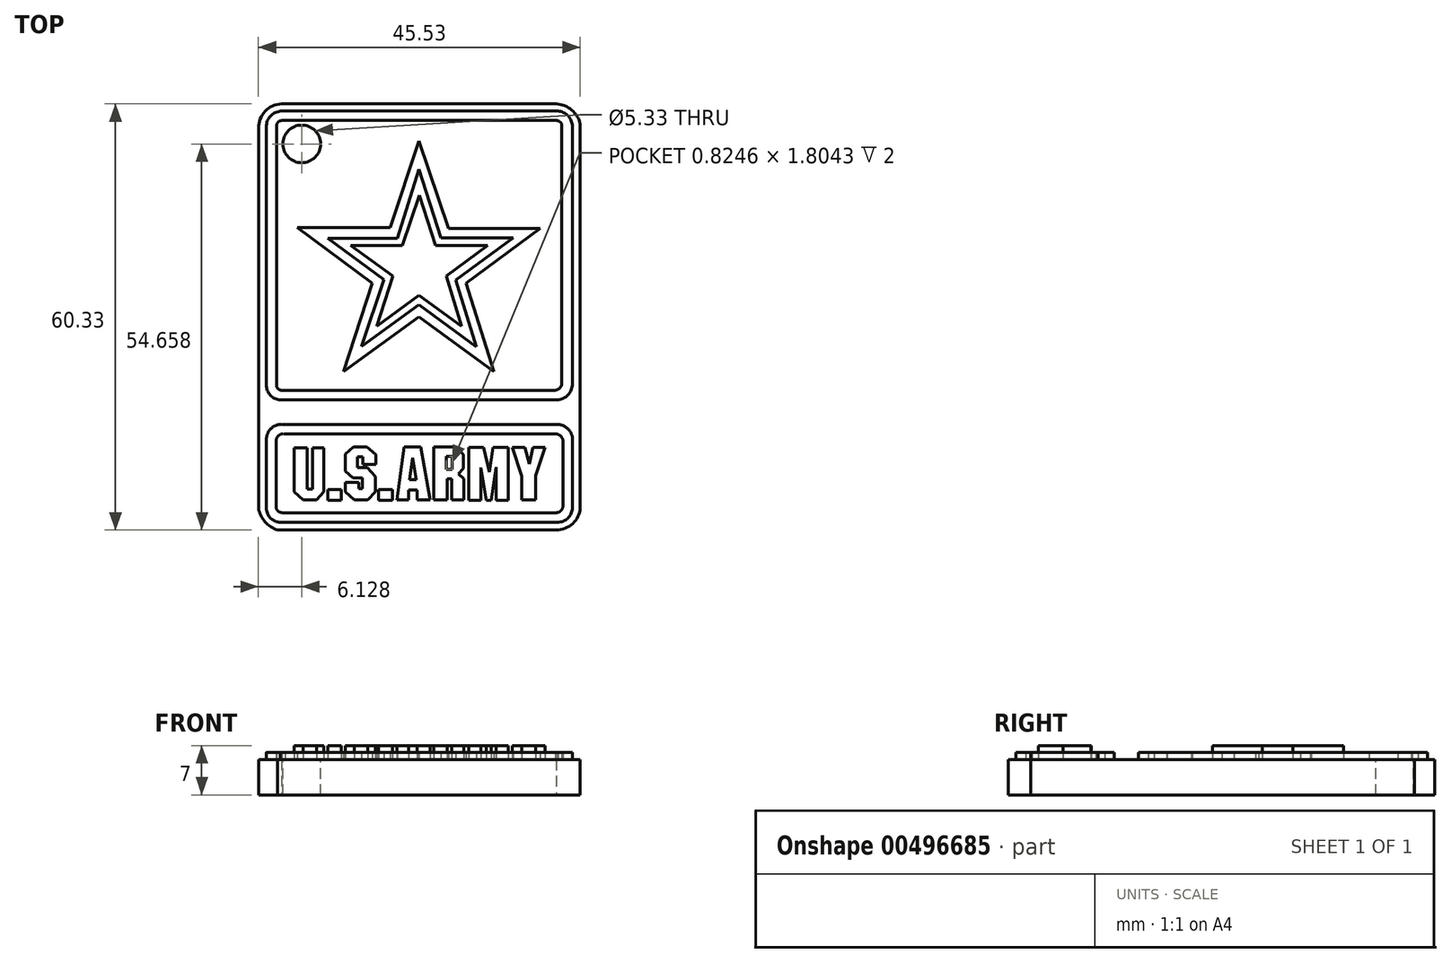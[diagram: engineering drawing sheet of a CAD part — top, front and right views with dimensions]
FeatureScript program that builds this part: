
annotation { "Feature Type Name" : "Feature", "Feature Type Description" : "" }
export const myFeature = defineFeature(function(context is Context, id is Id, definition is map)
    precondition{}
    {
        {
            var Q0;
            Q0=qCreatedBy(makeId("Top.planeOp"),FACE);
            var sketch = newSketch(context, id + "F0", { "sketchPlane" : qUnion([Q0])});
            skLineSegment(sketch, "E0", {"start": v(-59.52, 64.35) * mm, "end": v(-59.52, 10.5) * mm});
            skArc(sketch, "E1", {"start": v(-59.52, 10.5) * mm, "mid": v(-58.58, 8.6) * mm, "end": v(-56.8, 7.44) * mm});
            skLineSegment(sketch, "E2", {"start": v(-56.8, 7.44) * mm, "end": v(-17.38, 7.44) * mm});
            skArc(sketch, "E3", {"start": v(-17.38, 7.44) * mm, "mid": v(-15.06, 8.35) * mm, "end": v(-13.99, 10.6) * mm});
            skLineSegment(sketch, "E4", {"start": v(-13.99, 10.6) * mm, "end": v(-13.99, 64.9) * mm});
            skArc(sketch, "E5", {"start": v(-13.99, 64.9) * mm, "mid": v(-15.21, 66.9) * mm, "end": v(-17.38, 67.77) * mm});
            skLineSegment(sketch, "E6", {"start": v(-17.38, 67.77) * mm, "end": v(-56.25, 67.77) * mm});
            skArc(sketch, "E7", {"start": v(-56.25, 67.77) * mm, "mid": v(-58.57, 66.71) * mm, "end": v(-59.52, 64.35) * mm});
            skSolve(sketch);
        }
        {
            var Q0;
            Q0=makeQuery(id+"F0.imprint","IMPRINT",FACE,{"disambiguationData":[TD([[makeQuery(id+"F0.imprint","IMPRINT",EDGE,{"derivedFrom":sQuery(id+"F0.wireOp",EDGE,"E0")}),1.0]])]});
            var sketch = newSketch(context, id + "F1", { "sketchPlane" : qUnion([Q0])});
            skLineSegment(sketch, "E8", {"start": v(-58.4, 64.53) * mm, "end": v(-58.4, 28) * mm});
            skLineSegment(sketch, "E9", {"start": v(-56.4, 25.84) * mm, "end": v(-17.26, 25.84) * mm});
            skLineSegment(sketch, "E10", {"start": v(-15.1, 28.14) * mm, "end": v(-15.1, 64.56) * mm});
            skLineSegment(sketch, "E11", {"start": v(-17.16, 66.74) * mm, "end": v(-56.36, 66.74) * mm});
            skArc(sketch, "E12", {"start": v(-56.36, 66.74) * mm, "mid": v(-57.82, 66.04) * mm, "end": v(-58.4, 64.53) * mm});
            skArc(sketch, "E13", {"start": v(-58.4, 28) * mm, "mid": v(-57.83, 26.52) * mm, "end": v(-56.4, 25.84) * mm});
            skArc(sketch, "E14", {"start": v(-17.26, 25.84) * mm, "mid": v(-15.73, 26.57) * mm, "end": v(-15.1, 28.14) * mm});
            skArc(sketch, "E15", {"start": v(-15.1, 64.56) * mm, "mid": v(-15.7, 66.05) * mm, "end": v(-17.16, 66.74) * mm});
            skLineSegment(sketch, "E16", {"start": v(-56.18, 65.4) * mm, "end": v(-17.37, 65.4) * mm});
            skLineSegment(sketch, "E17", {"start": v(-16.61, 64.46) * mm, "end": v(-16.61, 28.23) * mm});
            skLineSegment(sketch, "E18", {"start": v(-17.54, 27.23) * mm, "end": v(-56.23, 27.23) * mm});
            skLineSegment(sketch, "E19", {"start": v(-56.96, 28.09) * mm, "end": v(-56.96, 64.55) * mm});
            skArc(sketch, "E20", {"start": v(-56.18, 65.4) * mm, "mid": v(-56.76, 65.15) * mm, "end": v(-56.96, 64.55) * mm});
            skArc(sketch, "E21", {"start": v(-16.61, 64.46) * mm, "mid": v(-16.76, 65.12) * mm, "end": v(-17.37, 65.4) * mm});
            skArc(sketch, "E22", {"start": v(-17.54, 27.23) * mm, "mid": v(-16.88, 27.55) * mm, "end": v(-16.61, 28.23) * mm});
            skArc(sketch, "E23", {"start": v(-56.96, 28.09) * mm, "mid": v(-56.8, 27.49) * mm, "end": v(-56.23, 27.23) * mm});
            skLineSegment(sketch, "E24", {"start": v(-36.85, 62.52) * mm, "end": v(-40.87, 50.28) * mm});
            skLineSegment(sketch, "E25", {"start": v(-40.87, 50.28) * mm, "end": v(-54.03, 50.28) * mm});
            skLineSegment(sketch, "E26", {"start": v(-54.03, 50.28) * mm, "end": v(-43.41, 42.41) * mm});
            skLineSegment(sketch, "E27", {"start": v(-43.41, 42.41) * mm, "end": v(-47.5, 29.85) * mm});
            skLineSegment(sketch, "E28", {"start": v(-47.5, 29.85) * mm, "end": v(-36.81, 37.65) * mm});
            skLineSegment(sketch, "E29", {"start": v(-36.81, 37.65) * mm, "end": v(-26.23, 29.88) * mm});
            skLineSegment(sketch, "E30", {"start": v(-26.23, 29.88) * mm, "end": v(-30.14, 42.41) * mm});
            skLineSegment(sketch, "E31", {"start": v(-30.14, 42.41) * mm, "end": v(-19.66, 50.14) * mm});
            skLineSegment(sketch, "E32", {"start": v(-19.66, 50.14) * mm, "end": v(-32.65, 50.14) * mm});
            skLineSegment(sketch, "E33", {"start": v(-32.65, 50.14) * mm, "end": v(-36.85, 62.52) * mm});
            skLineSegment(sketch, "E34", {"start": v(-36.85, 58.5) * mm, "end": v(-39.88, 48.76) * mm});
            skLineSegment(sketch, "E35", {"start": v(-39.88, 48.76) * mm, "end": v(-49.73, 48.76) * mm});
            skLineSegment(sketch, "E36", {"start": v(-49.73, 48.76) * mm, "end": v(-41.79, 42.87) * mm});
            skLineSegment(sketch, "E37", {"start": v(-41.79, 42.87) * mm, "end": v(-44.93, 33.45) * mm});
            skLineSegment(sketch, "E38", {"start": v(-44.93, 33.45) * mm, "end": v(-36.85, 39.34) * mm});
            skLineSegment(sketch, "E39", {"start": v(-36.85, 39.34) * mm, "end": v(-28.7, 33.36) * mm});
            skLineSegment(sketch, "E40", {"start": v(-28.7, 33.36) * mm, "end": v(-31.63, 42.83) * mm});
            skLineSegment(sketch, "E41", {"start": v(-31.63, 42.83) * mm, "end": v(-23.47, 48.78) * mm});
            skLineSegment(sketch, "E42", {"start": v(-23.47, 48.78) * mm, "end": v(-33.7, 48.78) * mm});
            skLineSegment(sketch, "E43", {"start": v(-33.7, 48.78) * mm, "end": v(-36.85, 58.5) * mm});
            skLineSegment(sketch, "E44", {"start": v(-56.16, 22.4) * mm, "end": v(-17.3, 22.4) * mm});
            skLineSegment(sketch, "E45", {"start": v(-15.07, 20.14) * mm, "end": v(-15.07, 10.61) * mm});
            skLineSegment(sketch, "E46", {"start": v(-17.27, 8.53) * mm, "end": v(-56.4, 8.53) * mm});
            skLineSegment(sketch, "E47", {"start": v(-58.4, 10.55) * mm, "end": v(-58.4, 20.29) * mm});
            skArc(sketch, "E48", {"start": v(-56.16, 22.4) * mm, "mid": v(-57.73, 21.83) * mm, "end": v(-58.4, 20.29) * mm});
            skArc(sketch, "E49", {"start": v(-15.07, 20.14) * mm, "mid": v(-15.7, 21.74) * mm, "end": v(-17.3, 22.4) * mm});
            skArc(sketch, "E50", {"start": v(-17.27, 8.53) * mm, "mid": v(-15.76, 9.14) * mm, "end": v(-15.07, 10.61) * mm});
            skArc(sketch, "E51", {"start": v(-58.4, 10.55) * mm, "mid": v(-57.81, 9.14) * mm, "end": v(-56.4, 8.53) * mm});
            skLineSegment(sketch, "E52", {"start": v(-57.03, 20.02) * mm, "end": v(-57.03, 10.79) * mm});
            skLineSegment(sketch, "E53", {"start": v(-56.17, 9.9) * mm, "end": v(-17.45, 9.9) * mm});
            skLineSegment(sketch, "E54", {"start": v(-16.44, 10.88) * mm, "end": v(-16.44, 19.81) * mm});
            skLineSegment(sketch, "E55", {"start": v(-17.53, 21.06) * mm, "end": v(-55.75, 21.06) * mm});
            skArc(sketch, "E56", {"start": v(-55.75, 21.06) * mm, "mid": v(-56.64, 20.84) * mm, "end": v(-57.03, 20.02) * mm});
            skArc(sketch, "E57", {"start": v(-57.03, 10.79) * mm, "mid": v(-56.79, 10.16) * mm, "end": v(-56.17, 9.9) * mm});
            skArc(sketch, "E58", {"start": v(-17.45, 9.9) * mm, "mid": v(-16.73, 10.18) * mm, "end": v(-16.44, 10.88) * mm});
            skArc(sketch, "E59", {"start": v(-16.44, 19.81) * mm, "mid": v(-16.7, 20.68) * mm, "end": v(-17.53, 21.06) * mm});
            skSolve(sketch);
        }
        {
            var Q0;
            Q0=makeQuery(id+"F0.imprint","IMPRINT",FACE,{"disambiguationData":[TD([[makeQuery(id+"F0.imprint","IMPRINT",EDGE,{"derivedFrom":sQuery(id+"F0.wireOp",EDGE,"E0")}),1.0]])]});
            var sketch = newSketch(context, id + "F2", { "sketchPlane" : qUnion([Q0])});
            skLineSegment(sketch, "E60", {"start": v(-36.76, 54.86) * mm, "end": v(-39.14, 47.7) * mm});
            skLineSegment(sketch, "E61", {"start": v(-39.14, 47.7) * mm, "end": v(-46.47, 47.7) * mm});
            skLineSegment(sketch, "E62", {"start": v(-46.47, 47.7) * mm, "end": v(-40.5, 43.37) * mm});
            skLineSegment(sketch, "E63", {"start": v(-40.5, 43.37) * mm, "end": v(-42.79, 36.3) * mm});
            skLineSegment(sketch, "E64", {"start": v(-42.79, 36.3) * mm, "end": v(-36.8, 40.7) * mm});
            skLineSegment(sketch, "E65", {"start": v(-36.8, 40.7) * mm, "end": v(-30.77, 36.3) * mm});
            skLineSegment(sketch, "E66", {"start": v(-30.77, 36.3) * mm, "end": v(-32.96, 43.37) * mm});
            skLineSegment(sketch, "E67", {"start": v(-32.96, 43.37) * mm, "end": v(-27.12, 47.7) * mm});
            skLineSegment(sketch, "E68", {"start": v(-27.12, 47.7) * mm, "end": v(-34.48, 47.7) * mm});
            skLineSegment(sketch, "E69", {"start": v(-34.48, 47.7) * mm, "end": v(-36.76, 54.86) * mm});
            skLineSegment(sketch, "E70", {"start": v(-54.45, 19.1) * mm, "end": v(-54.45, 12.84) * mm});
            skLineSegment(sketch, "E71", {"start": v(-54.45, 12.84) * mm, "end": v(-54.45, 19.1) * mm});
            skLineSegment(sketch, "E72", {"start": v(-54.45, 19.1) * mm, "end": v(-52.6, 19.1) * mm});
            skLineSegment(sketch, "E73", {"start": v(-52.6, 19.1) * mm, "end": v(-52.6, 13.26) * mm});
            skLineSegment(sketch, "E74", {"start": v(-52.6, 13.26) * mm, "end": v(-51.87, 13.26) * mm});
            skLineSegment(sketch, "E75", {"start": v(-51.87, 13.26) * mm, "end": v(-51.87, 19.1) * mm});
            skLineSegment(sketch, "E76", {"start": v(-51.87, 19.1) * mm, "end": v(-50.25, 19.1) * mm});
            skLineSegment(sketch, "E77", {"start": v(-50.25, 19.1) * mm, "end": v(-50.25, 12.84) * mm});
            skLineSegment(sketch, "E78", {"start": v(-51.32, 11.7) * mm, "end": v(-53.21, 11.7) * mm});
            skLineSegment(sketch, "E79", {"start": v(-49.69, 13.2) * mm, "end": v(-49.69, 11.67) * mm});
            skLineSegment(sketch, "E80", {"start": v(-49.69, 11.67) * mm, "end": v(-47.78, 11.67) * mm});
            skLineSegment(sketch, "E81", {"start": v(-49.69, 13.2) * mm, "end": v(-47.8, 13.2) * mm});
            skLineSegment(sketch, "E82", {"start": v(-47.8, 13.2) * mm, "end": v(-47.78, 11.67) * mm});
            skLineSegment(sketch, "E83", {"start": v(-42.51, 13.2) * mm, "end": v(-42.51, 11.67) * mm});
            skLineSegment(sketch, "E84", {"start": v(-42.51, 11.67) * mm, "end": v(-40.54, 11.67) * mm});
            skLineSegment(sketch, "E85", {"start": v(-40.54, 11.67) * mm, "end": v(-40.54, 13.2) * mm});
            skLineSegment(sketch, "E86", {"start": v(-40.54, 13.2) * mm, "end": v(-42.51, 13.2) * mm});
            skLineSegment(sketch, "E87", {"start": v(-29.77, 19.11) * mm, "end": v(-29.77, 11.67) * mm});
            skLineSegment(sketch, "E88", {"start": v(-29.77, 11.67) * mm, "end": v(-28.05, 11.67) * mm});
            skLineSegment(sketch, "E89", {"start": v(-28.05, 11.67) * mm, "end": v(-28.05, 16.26) * mm});
            skLineSegment(sketch, "E90", {"start": v(-28.05, 16.26) * mm, "end": v(-27.3, 11.67) * mm});
            skLineSegment(sketch, "E91", {"start": v(-27.3, 11.67) * mm, "end": v(-26.6, 11.67) * mm});
            skLineSegment(sketch, "E92", {"start": v(-26.6, 11.67) * mm, "end": v(-25.9, 16.34) * mm});
            skLineSegment(sketch, "E93", {"start": v(-25.9, 16.34) * mm, "end": v(-25.9, 11.67) * mm});
            skLineSegment(sketch, "E94", {"start": v(-25.9, 11.67) * mm, "end": v(-24.2, 11.67) * mm});
            skLineSegment(sketch, "E95", {"start": v(-24.2, 11.67) * mm, "end": v(-24.2, 19.16) * mm});
            skLineSegment(sketch, "E96", {"start": v(-24.2, 19.16) * mm, "end": v(-26.33, 19.16) * mm});
            skLineSegment(sketch, "E97", {"start": v(-26.33, 19.16) * mm, "end": v(-26.84, 15.63) * mm});
            skLineSegment(sketch, "E98", {"start": v(-26.84, 15.63) * mm, "end": v(-27.7, 19.16) * mm});
            skLineSegment(sketch, "E99", {"start": v(-27.7, 19.16) * mm, "end": v(-29.77, 19.11) * mm});
            skLineSegment(sketch, "E100", {"start": v(-23.63, 19.16) * mm, "end": v(-21.8, 19.16) * mm});
            skLineSegment(sketch, "E101", {"start": v(-21.8, 19.16) * mm, "end": v(-21.22, 16.76) * mm});
            skLineSegment(sketch, "E102", {"start": v(-21.22, 16.76) * mm, "end": v(-20.69, 19.11) * mm});
            skLineSegment(sketch, "E103", {"start": v(-20.69, 19.11) * mm, "end": v(-18.95, 19.11) * mm});
            skLineSegment(sketch, "E104", {"start": v(-18.95, 19.11) * mm, "end": v(-20.31, 15.17) * mm});
            skLineSegment(sketch, "E105", {"start": v(-20.31, 15.17) * mm, "end": v(-20.31, 11.7) * mm});
            skLineSegment(sketch, "E106", {"start": v(-20.31, 11.7) * mm, "end": v(-22.24, 11.7) * mm});
            skLineSegment(sketch, "E107", {"start": v(-22.24, 11.7) * mm, "end": v(-22.24, 15.1) * mm});
            skLineSegment(sketch, "E108", {"start": v(-22.24, 15.1) * mm, "end": v(-23.63, 19.16) * mm});
            skLineSegment(sketch, "E109", {"start": v(-54.45, 12.84) * mm, "end": v(-53.21, 11.7) * mm});
            skLineSegment(sketch, "E110", {"start": v(-51.32, 11.7) * mm, "end": v(-50.25, 12.84) * mm});
            skLineSegment(sketch, "E111", {"start": v(-46.06, 19.2) * mm, "end": v(-44.19, 19.2) * mm});
            skLineSegment(sketch, "E112", {"start": v(-44.19, 19.2) * mm, "end": v(-42.93, 18.13) * mm});
            skLineSegment(sketch, "E113", {"start": v(-42.93, 18.13) * mm, "end": v(-42.93, 16.74) * mm});
            skLineSegment(sketch, "E114", {"start": v(-42.93, 16.74) * mm, "end": v(-44.73, 16.74) * mm});
            skLineSegment(sketch, "E115", {"start": v(-44.73, 16.74) * mm, "end": v(-44.73, 17.81) * mm});
            skLineSegment(sketch, "E116", {"start": v(-44.73, 17.81) * mm, "end": v(-45.51, 17.81) * mm});
            skLineSegment(sketch, "E117", {"start": v(-45.51, 17.81) * mm, "end": v(-45.51, 16.28) * mm});
            skLineSegment(sketch, "E118", {"start": v(-45.51, 16.28) * mm, "end": v(-44.15, 16.28) * mm});
            skLineSegment(sketch, "E119", {"start": v(-44.15, 16.28) * mm, "end": v(-42.95, 15) * mm});
            skLineSegment(sketch, "E120", {"start": v(-42.95, 15) * mm, "end": v(-42.95, 12.84) * mm});
            skLineSegment(sketch, "E121", {"start": v(-42.95, 12.84) * mm, "end": v(-44.04, 11.7) * mm});
            skLineSegment(sketch, "E122", {"start": v(-44.04, 11.7) * mm, "end": v(-45.93, 11.7) * mm});
            skLineSegment(sketch, "E123", {"start": v(-45.93, 11.7) * mm, "end": v(-47.21, 12.84) * mm});
            skLineSegment(sketch, "E124", {"start": v(-47.21, 12.84) * mm, "end": v(-47.21, 14.16) * mm});
            skLineSegment(sketch, "E125", {"start": v(-47.21, 14.16) * mm, "end": v(-45.32, 14.16) * mm});
            skLineSegment(sketch, "E126", {"start": v(-45.32, 14.16) * mm, "end": v(-45.32, 13.3) * mm});
            skLineSegment(sketch, "E127", {"start": v(-45.32, 13.3) * mm, "end": v(-44.84, 13.3) * mm});
            skLineSegment(sketch, "E128", {"start": v(-44.84, 13.3) * mm, "end": v(-44.84, 14.81) * mm});
            skLineSegment(sketch, "E129", {"start": v(-44.84, 14.81) * mm, "end": v(-46.14, 14.81) * mm});
            skLineSegment(sketch, "E130", {"start": v(-46.14, 14.81) * mm, "end": v(-47.21, 15.78) * mm});
            skLineSegment(sketch, "E131", {"start": v(-47.21, 15.78) * mm, "end": v(-47.21, 18.2) * mm});
            skLineSegment(sketch, "E132", {"start": v(-47.21, 18.2) * mm, "end": v(-46.06, 19.2) * mm});
            skLineSegment(sketch, "E133", {"start": v(-38.94, 19.2) * mm, "end": v(-36.53, 19.2) * mm});
            skLineSegment(sketch, "E134", {"start": v(-36.53, 19.2) * mm, "end": v(-35.2, 11.7) * mm});
            skLineSegment(sketch, "E135", {"start": v(-35.2, 11.7) * mm, "end": v(-37.05, 11.7) * mm});
            skLineSegment(sketch, "E136", {"start": v(-37.05, 11.7) * mm, "end": v(-37.05, 13.1) * mm});
            skLineSegment(sketch, "E137", {"start": v(-37.05, 13.1) * mm, "end": v(-38.25, 13.1) * mm});
            skLineSegment(sketch, "E138", {"start": v(-38.25, 13.1) * mm, "end": v(-38.25, 11.7) * mm});
            skLineSegment(sketch, "E139", {"start": v(-38.25, 11.7) * mm, "end": v(-39.95, 11.7) * mm});
            skLineSegment(sketch, "E140", {"start": v(-39.95, 11.7) * mm, "end": v(-38.94, 19.2) * mm});
            skLineSegment(sketch, "E141", {"start": v(-34.73, 19.2) * mm, "end": v(-34.73, 11.7) * mm});
            skLineSegment(sketch, "E142", {"start": v(-34.73, 11.7) * mm, "end": v(-32.84, 11.7) * mm});
            skLineSegment(sketch, "E143", {"start": v(-32.84, 11.7) * mm, "end": v(-32.84, 14.69) * mm});
            skLineSegment(sketch, "E144", {"start": v(-32.84, 14.69) * mm, "end": v(-32.19, 14.69) * mm});
            skLineSegment(sketch, "E145", {"start": v(-32.19, 14.69) * mm, "end": v(-32.19, 11.7) * mm});
            skLineSegment(sketch, "E146", {"start": v(-32.19, 11.7) * mm, "end": v(-30.49, 11.7) * mm});
            skLineSegment(sketch, "E147", {"start": v(-30.49, 11.7) * mm, "end": v(-30.49, 14.73) * mm});
            skLineSegment(sketch, "E148", {"start": v(-30.49, 14.73) * mm, "end": v(-31.24, 15.4) * mm});
            skLineSegment(sketch, "E149", {"start": v(-31.24, 15.4) * mm, "end": v(-30.55, 16.17) * mm});
            skLineSegment(sketch, "E150", {"start": v(-30.55, 16.17) * mm, "end": v(-30.55, 18.13) * mm});
            skLineSegment(sketch, "E151", {"start": v(-30.55, 18.13) * mm, "end": v(-31.66, 19.2) * mm});
            skLineSegment(sketch, "E152", {"start": v(-31.66, 19.2) * mm, "end": v(-34.73, 19.2) * mm});
            skLineSegment(sketch, "E153", {"start": v(-37.7, 17.65) * mm, "end": v(-38.13, 14.56) * mm});
            skLineSegment(sketch, "E154", {"start": v(-38.13, 14.56) * mm, "end": v(-37.21, 14.56) * mm});
            skLineSegment(sketch, "E155", {"start": v(-37.21, 14.56) * mm, "end": v(-37.7, 17.65) * mm});
            skLineSegment(sketch, "E156", {"start": v(-32.94, 17.85) * mm, "end": v(-32.94, 16.05) * mm});
            skLineSegment(sketch, "E157", {"start": v(-32.94, 16.05) * mm, "end": v(-32.12, 16.05) * mm});
            skLineSegment(sketch, "E158", {"start": v(-32.12, 16.05) * mm, "end": v(-32.12, 17.85) * mm});
            skLineSegment(sketch, "E159", {"start": v(-32.12, 17.85) * mm, "end": v(-32.94, 17.85) * mm});
            skSolve(sketch);
        }
        {
            var Q0;
            Q0 = qSketchRegion(id + "F0", true);
            extrude(context, id + "F3", {"entities" : qUnion([Q0]), "depth" : 5 * mm, "offsetDistance" : 25 * mm});
        }
        {
            var Q0;
            Q0 = qSketchRegion(id + "F2", true);
            extrude(context, id + "F4", {"entities" : qUnion([Q0]), "operationType" : NewBodyOperationType.ADD, "depth" : 7 * mm, "offsetDistance" : 25 * mm});
        }
        {
            var Q0;
            Q0=makeQuery(id+"F1.imprint","IMPRINT",FACE,{"disambiguationData":[TD([[makeQuery(id+"F1.imprint","IMPRINT",EDGE,{"derivedFrom":sQuery(id+"F1.wireOp",EDGE,"E8")}),1.0]])]});
            var Q1;
            Q1=makeQuery(id+"F1.imprint","IMPRINT",FACE,{"disambiguationData":[TD([[makeQuery(id+"F1.imprint","IMPRINT",EDGE,{"derivedFrom":sQuery(id+"F1.wireOp",EDGE,"E24")}),1.0]])]});
            var Q2;
            Q2=makeQuery(id+"F1.imprint","IMPRINT",FACE,{"disambiguationData":[TD([[makeQuery(id+"F1.imprint","IMPRINT",EDGE,{"derivedFrom":sQuery(id+"F1.wireOp",EDGE,"E44")}),-1.0]])]});
            extrude(context, id + "F5", {"entities" : qUnion([Q0, Q1, Q2]), "operationType" : NewBodyOperationType.ADD, "depth" : 6 * mm, "offsetDistance" : 25 * mm});
        }
        {
            var Q0;
            {var subQ0=sQuery(id+"F0.wireOp",EDGE,"E2");var subQ1=sQuery(id+"F0.wireOp",EDGE,"E1");var subQ2=sQuery(id+"F0.wireOp",EDGE,"E3");var subQ3=sQuery(id+"F0.wireOp",EDGE,"E0");var subQ4=sQuery(id+"F0.wireOp",EDGE,"E5");var subQ5=sQuery(id+"F0.wireOp",EDGE,"E6");var subQ6=sQuery(id+"F0.wireOp",EDGE,"E4");var subQ7=sQuery(id+"F0.wireOp",EDGE,"E7");Q0=makeQuery(id+"F5.boolean.opBoolean","SPLIT",FACE,{"disambiguationData":[TD([makeQuery(id+"F5.opExtrude","SWEPT_FACE",FACE,{"disambiguationData":[OSD([sQuery(id+"F1.wireOp",EDGE,"E16")])]})])],"derivedFrom":makeQuery(id+"F4.boolean.opBoolean","SPLIT",FACE,{"disambiguationData":[TD([makeQuery(id+"F3.opExtrude","SWEPT_FACE",FACE,{"disambiguationData":[OSD([subQ3])]})])],"derivedFrom":makeQuery(id+"F3.opExtrude","CAP_FACE",FACE,{"disambiguationData":[OSD([subQ3,subQ1,subQ0,subQ2,subQ6,subQ4,subQ5,subQ7])],"isStart":false})})});}
            var sketch = newSketch(context, id + "F6", { "sketchPlane" : qUnion([Q0])});
            skCircle(sketch, "E160", {"center": v(-53.4, 62.1) * mm, "radius": 2.67 * mm});
            skSolve(sketch);
        }
        {
            var Q0;
            Q0 = qSketchRegion(id + "F6", true);
            extrude(context, id + "F7", {"entities" : qUnion([Q0]), "operationType" : NewBodyOperationType.REMOVE, "oppositeDirection" : true, "depth" : 25 * mm, "offsetDistance" : 25 * mm});
        }
    });
